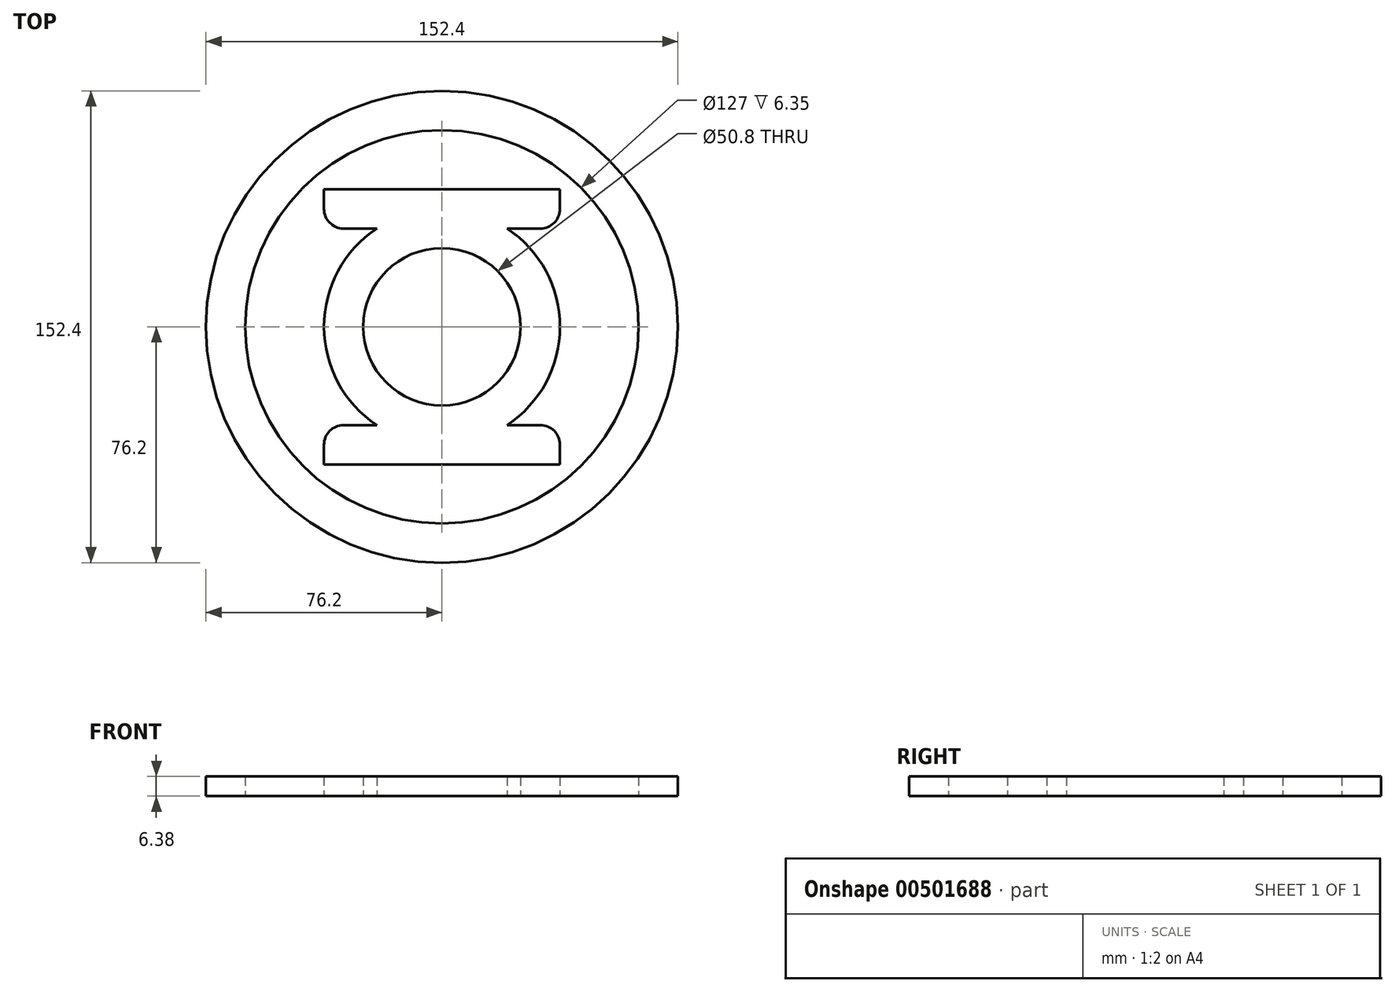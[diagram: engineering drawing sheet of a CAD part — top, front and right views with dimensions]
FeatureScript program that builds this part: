
annotation { "Feature Type Name" : "Feature", "Feature Type Description" : "" }
export const myFeature = defineFeature(function(context is Context, id is Id, definition is map)
    precondition{}
    {
        {
            var Q0;
            Q0=qCreatedBy(makeId("Top.planeOp"),FACE);
            var sketch = newSketch(context, id + "F0", { "sketchPlane" : qUnion([Q0])});
            skCircle(sketch, "E0", {"center": v(0, 0) * mm, "radius": 63.5 * mm});
            skSolve(sketch);
        }
        {
            var Q0;
            Q0 = qSketchRegion(id + "F0", true);
            extrude(context, id + "F1", {"entities" : qUnion([Q0]), "depth" : 0.03 * mm});
        }
        {
            var Q0;
            Q0=makeQuery(id+"F1.opExtrude","CAP_FACE",FACE,{"disambiguationData":[OSD([sQuery(id+"F0.wireOp",EDGE,"E0")])],"isStart":false});
            var sketch = newSketch(context, id + "F2", { "sketchPlane" : qUnion([Q0])});
            skCircle(sketch, "E1", {"center": v(0, 0) * mm, "radius": 38.1 * mm});
            skLineSegment(sketch, "E2", {"start": v(0, 31.75) * mm, "end": v(-31.75, 31.75) * mm});
            skLineSegment(sketch, "E3", {"start": v(-38.1, 38.1) * mm, "end": v(-38.1, 44.45) * mm});
            skLineSegment(sketch, "E4", {"start": v(-38.1, 44.45) * mm, "end": v(38.1, 44.45) * mm});
            skLineSegment(sketch, "E5", {"start": v(31.75, 31.75) * mm, "end": v(0, 31.75) * mm});
            skLineSegment(sketch, "E6", {"start": v(0, -31.75) * mm, "end": v(31.75, -31.75) * mm});
            skLineSegment(sketch, "E7", {"start": v(38.1, -38.1) * mm, "end": v(38.1, -44.45) * mm});
            skLineSegment(sketch, "E8", {"start": v(38.1, -44.45) * mm, "end": v(-38.1, -44.45) * mm});
            skLineSegment(sketch, "E9", {"start": v(-38.1, -44.45) * mm, "end": v(-38.1, -38.1) * mm});
            skLineSegment(sketch, "E10", {"start": v(-31.75, -31.75) * mm, "end": v(0, -31.75) * mm});
            skCircle(sketch, "E11", {"center": v(0, 0) * mm, "radius": 25.4 * mm});
            skLineSegment(sketch, "E12", {"start": v(38.1, 44.45) * mm, "end": v(38.1, 38.1) * mm});
            skPoint(sketch, "E13.visualSharp", {"position": v(-38.1, 31.75) * mm});
            skArc(sketch, "E13.filletArc", {"start": v(-38.1, 38.1) * mm, "mid": v(-36.24, 33.6) * mm, "end": v(-31.75, 31.75) * mm});
            skPoint(sketch, "E14.visualSharp", {"position": v(38.1, 31.75) * mm});
            skArc(sketch, "E14.filletArc", {"start": v(31.75, 31.75) * mm, "mid": v(36.24, 33.6) * mm, "end": v(38.1, 38.1) * mm});
            skPoint(sketch, "E15.visualSharp", {"position": v(38.1, -31.75) * mm});
            skArc(sketch, "E15.filletArc", {"start": v(38.1, -38.1) * mm, "mid": v(36.24, -33.6) * mm, "end": v(31.75, -31.75) * mm});
            skPoint(sketch, "E16.visualSharp", {"position": v(-38.1, -31.75) * mm});
            skArc(sketch, "E16.filletArc", {"start": v(-31.75, -31.75) * mm, "mid": v(-36.24, -33.6) * mm, "end": v(-38.1, -38.1) * mm});
            skSolve(sketch);
        }
        {
            var Q0;
            Q0 = qSketchRegion(id + "F2", true);
            extrude(context, id + "F3", {"entities" : qUnion([Q0]), "depth" : 6.35 * mm});
        }
        {
            var Q0;
            Q0=qCreatedBy(makeId("Top.planeOp"),FACE);
            var sketch = newSketch(context, id + "F4", { "sketchPlane" : qUnion([Q0])});
            skCircle(sketch, "E17", {"center": v(0, 0) * mm, "radius": 76.2 * mm});
            skCircle(sketch, "E18", {"center": v(0, 0) * mm, "radius": 63.5 * mm});
            skSolve(sketch);
        }
        {
            var Q0;
            Q0=makeQuery(id+"F4.imprint","IMPRINT",FACE,{"disambiguationData":[TD([[makeQuery(id+"F4.imprint","IMPRINT",EDGE,{"derivedFrom":sQuery(id+"F4.wireOp",EDGE,"E17")}),1.0]])]});
            extrude(context, id + "F5", {"entities" : qUnion([Q0]), "depth" : 6.35 * mm});
        }
    });
